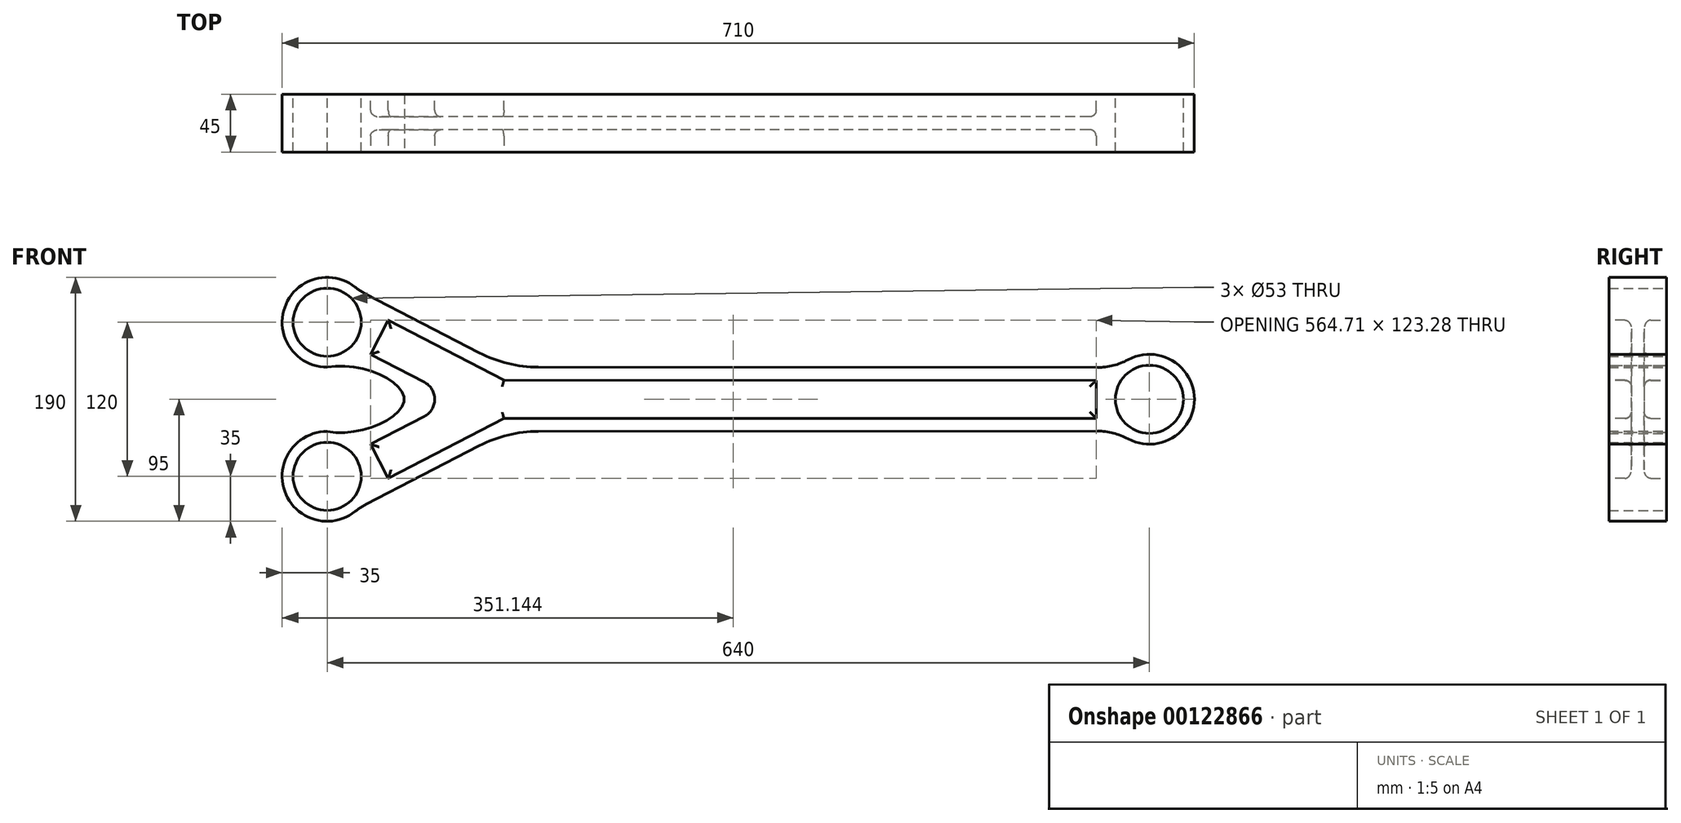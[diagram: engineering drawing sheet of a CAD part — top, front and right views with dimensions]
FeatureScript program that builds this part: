
annotation { "Feature Type Name" : "Feature", "Feature Type Description" : "" }
export const myFeature = defineFeature(function(context is Context, id is Id, definition is map)
    precondition{}
    {
        {
            var Q0;
            Q0=qCreatedBy(makeId("Front.planeOp"),FACE);
            var sketch = newSketch(context, id + "F0", { "sketchPlane" : qUnion([Q0])});
            skArc(sketch, "E0", {"start": v(-16.66, -30.78) * mm, "mid": v(35, 0) * mm, "end": v(-16.66, 30.78) * mm});
            skArc(sketch, "E1", {"start": v(-618.13, 87.33) * mm, "mid": v(-673.03, 71.59) * mm, "end": v(-640, 25) * mm});
            skCircle(sketch, "E2", {"center": v(-700, 0) * mm, "radius": 27.5 * mm, "construction": true});
            skCircle(sketch, "E3", {"center": v(-640, 60) * mm, "radius": 26.5 * mm});
            skCircle(sketch, "E4", {"center": v(-640, -60) * mm, "radius": 26.5 * mm});
            skCircle(sketch, "E5", {"center": v(0, 0) * mm, "radius": 26.5 * mm});
            skLineSegment(sketch, "E6", {"start": v(-40.48, 24.76) * mm, "end": v(-475.65, 24.99) * mm});
            skLineSegment(sketch, "E7", {"start": v(-40.48, -24.76) * mm, "end": v(-475.65, -24.99) * mm});
            skLineSegment(sketch, "E8", {"start": v(-521.62, -36.2) * mm, "end": v(-609.9, -81.98) * mm});
            skLineSegment(sketch, "E9", {"start": v(-521.62, 36.2) * mm, "end": v(-609.9, 81.98) * mm});
            skPoint(sketch, "E10.visualSharp", {"position": v(-500, 25) * mm});
            skArc(sketch, "E10.filletArc", {"start": v(-521.62, 36.2) * mm, "mid": v(-499.3, 27.84) * mm, "end": v(-475.65, 24.99) * mm});
            skPoint(sketch, "E11.visualSharp", {"position": v(-500, -25) * mm});
            skArc(sketch, "E11.filletArc", {"start": v(-475.65, -24.99) * mm, "mid": v(-499.3, -27.84) * mm, "end": v(-521.62, -36.2) * mm});
            skPoint(sketch, "E12.visualSharp", {"position": v(-615.25, 84.75) * mm});
            skArc(sketch, "E13", {"start": v(-640, -25) * mm, "mid": v(-673.03, -71.59) * mm, "end": v(-618.13, -87.33) * mm});
            skFitSpline(sketch, "E14", {"points": [v(-640, -25) * mm, v(-580, 0) * mm, v(-640, 25) * mm], "startDerivative": vector(150, -30) * mm, "endDerivative": vector(-150, -30) * mm});
            skPoint(sketch, "E15.visualSharp", {"position": v(-615.25, -84.75) * mm});
            skLineSegment(sketch, "E16", {"start": v(-24.75, 24.75) * mm, "end": v(0, 0) * mm, "construction": true});
            skLineSegment(sketch, "E17", {"start": v(-24.75, -24.75) * mm, "end": v(0, 0) * mm, "construction": true});
            skPoint(sketch, "E18.visualSharp", {"position": v(-24.75, 24.75) * mm});
            skArc(sketch, "E18.filletArc", {"start": v(-40.48, 24.76) * mm, "mid": v(-28.2, 26.28) * mm, "end": v(-16.66, 30.78) * mm});
            skPoint(sketch, "E19.visualSharp", {"position": v(-24.75, -24.75) * mm});
            skArc(sketch, "E19.filletArc", {"start": v(-16.66, -30.78) * mm, "mid": v(-28.2, -26.28) * mm, "end": v(-40.48, -24.76) * mm});
            skLineSegment(sketch, "E20", {"start": v(-615.25, 84.75) * mm, "end": v(-640, 60) * mm, "construction": true});
            skLineSegment(sketch, "E21", {"start": v(-640, -60) * mm, "end": v(-640, 177.49) * mm, "construction": true});
            skArc(sketch, "E22.filletArc", {"start": v(-618.13, 87.33) * mm, "mid": v(-614.15, 84.45) * mm, "end": v(-609.9, 81.98) * mm});
            skLineSegment(sketch, "E23", {"start": v(-615.25, -84.75) * mm, "end": v(-640, -60) * mm, "construction": true});
            skArc(sketch, "E24.filletArc", {"start": v(-609.9, -81.98) * mm, "mid": v(-614.15, -84.45) * mm, "end": v(-618.13, -87.33) * mm});
            skSolve(sketch);
        }
        {
            var Q0;
            Q0=qSketchRegion(id+"F0",true);
            extrude(context, id + "F1", {"entities" : qUnion([Q0]), "depth" : 45 * mm});
        }
        {
            var Q0;
            Q0=makeQuery(id+"F1.opExtrude","SWEPT_BODY",BODY,{"disambiguationData":[OSD([sQuery(id+"F0.wireOp",EDGE,"E0"),sQuery(id+"F0.wireOp",EDGE,"E1"),sQuery(id+"F0.wireOp",EDGE,"hKVllitM-rUlu-PjKN-B9u5-COeOs3Kio4uB"),sQuery(id+"F0.wireOp",EDGE,"bIEpRebq-8nbQ-7rQF-Jdrm-i3E8cfRsBNN9"),sQuery(id+"F0.wireOp",EDGE,"ymSRshFr-buK2-GFJu-27zL-H9ECYoIg19t0"),sQuery(id+"F0.wireOp",EDGE,"e6450e41-44a2-4cb5-af14-4686bec827bc"),sQuery(id+"F0.wireOp",EDGE,"ipdW7DlG-pZfv-p4Vr-qYAQ-uRQYnpMPVyQN"),sQuery(id+"F0.wireOp",EDGE,"9qNpO7d9-6r7V-397W-DIXA-CVevZtzhY8f4"),sQuery(id+"F0.wireOp",EDGE,"E3"),sQuery(id+"F0.wireOp",EDGE,"E4"),sQuery(id+"F0.wireOp",EDGE,"E5")])]});
            var Q1;
            Q1=makeQuery(id+"F1.opExtrude","CAP_EDGE",EDGE,{"disambiguationData":[OSD([sQuery(id+"F0.wireOp",EDGE,"E5")])],"isStart":false});
            transform(context, id + "F2", {"entities" : qUnion([Q0]), "transformType" : TransformType.ROTATION, "transformAxis" : qUnion([Q1]), "angle" : 12.5 * degree, "makeCopy" : true});
        }
        {
            var Q0;
            Q0=makeQuery(id+"F1.opExtrude","CAP_FACE",FACE,{"disambiguationData":[OSD([sQuery(id+"F0.wireOp",EDGE,"E0"),sQuery(id+"F0.wireOp",EDGE,"E1"),sQuery(id+"F0.wireOp",EDGE,"E3"),sQuery(id+"F0.wireOp",EDGE,"E4"),sQuery(id+"F0.wireOp",EDGE,"E5"),sQuery(id+"F0.wireOp",EDGE,"E6"),sQuery(id+"F0.wireOp",EDGE,"E7"),sQuery(id+"F0.wireOp",EDGE,"E8"),sQuery(id+"F0.wireOp",EDGE,"E9"),sQuery(id+"F0.wireOp",EDGE,"E10.filletArc"),sQuery(id+"F0.wireOp",EDGE,"E11.filletArc"),sQuery(id+"F0.wireOp",EDGE,"E13"),sQuery(id+"F0.wireOp",EDGE,"E14"),sQuery(id+"F0.wireOp",EDGE,"E18.filletArc"),sQuery(id+"F0.wireOp",EDGE,"E19.filletArc"),sQuery(id+"F0.wireOp",EDGE,"E22.filletArc"),sQuery(id+"F0.wireOp",EDGE,"E24.filletArc")])],"isStart":false});
            var sketch = newSketch(context, id + "F3", { "sketchPlane" : qUnion([Q0])});
            skLineSegment(sketch, "E25", {"start": v(-41.5, 14.76) * mm, "end": v(-502.44, 15) * mm});
            skLineSegment(sketch, "E26", {"start": v(-41.5, -14.76) * mm, "end": v(-502.44, -15) * mm});
            skLineSegment(sketch, "E27", {"start": v(-502.44, -15) * mm, "end": v(-592.4, -61.64) * mm});
            skLineSegment(sketch, "E28", {"start": v(-592.4, -61.64) * mm, "end": v(-606.21, -35) * mm});
            skLineSegment(sketch, "E29", {"start": v(-606.21, -35) * mm, "end": v(-564.37, -13.32) * mm});
            skLineSegment(sketch, "E30", {"start": v(-502.44, 15) * mm, "end": v(-592.4, 61.64) * mm});
            skLineSegment(sketch, "E31", {"start": v(-592.4, 61.64) * mm, "end": v(-606.21, 35) * mm});
            skLineSegment(sketch, "E32", {"start": v(-606.21, 35) * mm, "end": v(-564.37, 13.32) * mm});
            skPoint(sketch, "E33.visualSharp", {"position": v(-538.69, 0) * mm});
            skArc(sketch, "E33.filletArc", {"start": v(-564.37, -13.32) * mm, "mid": v(-556.28, 0) * mm, "end": v(-564.37, 13.32) * mm});
            skLineSegment(sketch, "E34", {"start": v(-41.5, 14.76) * mm, "end": v(-41.5, -14.76) * mm});
            skSolve(sketch);
        }
        {
            var Q0;
            Q0=qSketchRegion(id+"F3",true);
            extrude(context, id + "F4", {"entities" : qUnion([Q0]), "operationType" : NewBodyOperationType.REMOVE, "oppositeDirection" : true, "depth" : 17.5 * mm});
        }
        {
            var Q0;
            Q0=makeQuery(id+"F1.opExtrude","CAP_FACE",FACE,{"disambiguationData":[OSD([sQuery(id+"F0.wireOp",EDGE,"E0"),sQuery(id+"F0.wireOp",EDGE,"E1"),sQuery(id+"F0.wireOp",EDGE,"E3"),sQuery(id+"F0.wireOp",EDGE,"E4"),sQuery(id+"F0.wireOp",EDGE,"E5"),sQuery(id+"F0.wireOp",EDGE,"E6"),sQuery(id+"F0.wireOp",EDGE,"E7"),sQuery(id+"F0.wireOp",EDGE,"E8"),sQuery(id+"F0.wireOp",EDGE,"E9"),sQuery(id+"F0.wireOp",EDGE,"E10.filletArc"),sQuery(id+"F0.wireOp",EDGE,"E11.filletArc"),sQuery(id+"F0.wireOp",EDGE,"E13"),sQuery(id+"F0.wireOp",EDGE,"E14"),sQuery(id+"F0.wireOp",EDGE,"E18.filletArc"),sQuery(id+"F0.wireOp",EDGE,"E19.filletArc"),sQuery(id+"F0.wireOp",EDGE,"E22.filletArc"),sQuery(id+"F0.wireOp",EDGE,"E24.filletArc")])],"isStart":true});
            var sketch = newSketch(context, id + "F5", { "sketchPlane" : qUnion([Q0])});
            skLineSegment(sketch, "E35", {"start": v(41.5, 14.76) * mm, "end": v(502.44, 15) * mm});
            skLineSegment(sketch, "E36", {"start": v(502.44, 15) * mm, "end": v(592.4, 61.64) * mm});
            skLineSegment(sketch, "E37", {"start": v(592.4, 61.64) * mm, "end": v(606.21, 35) * mm});
            skLineSegment(sketch, "E38", {"start": v(606.21, -35) * mm, "end": v(592.4, -61.64) * mm});
            skLineSegment(sketch, "E39", {"start": v(592.4, -61.64) * mm, "end": v(502.44, -15) * mm});
            skLineSegment(sketch, "E40", {"start": v(502.44, -15) * mm, "end": v(41.5, -14.76) * mm});
            skLineSegment(sketch, "E41", {"start": v(41.5, 14.76) * mm, "end": v(41.5, -14.76) * mm});
            skLineSegment(sketch, "E42", {"start": v(606.21, 35) * mm, "end": v(564.37, 13.32) * mm});
            skLineSegment(sketch, "E43", {"start": v(564.37, -13.32) * mm, "end": v(606.21, -35) * mm});
            skPoint(sketch, "E44.visualSharp", {"position": v(538.69, 0) * mm});
            skArc(sketch, "E44.filletArc", {"start": v(564.37, 13.32) * mm, "mid": v(556.28, 0) * mm, "end": v(564.37, -13.32) * mm});
            skSolve(sketch);
        }
        {
            var Q0;
            Q0=qSketchRegion(id+"F5",true);
            extrude(context, id + "F6", {"entities" : qUnion([Q0]), "operationType" : NewBodyOperationType.REMOVE, "oppositeDirection" : true, "depth" : 17.5 * mm});
        }
        {
            var Q0;
            Q0=makeQuery(id+"F6.boolean.opBoolean","COPY",EDGE,{"derivedFrom":makeQuery(id+"F6.opExtrude","CAP_EDGE",EDGE,{"disambiguationData":[OSD([sQuery(id+"F5.wireOp",EDGE,"E35")])],"isStart":false})});
            var Q1;
            Q1=makeQuery(id+"F6.boolean.opBoolean","COPY",EDGE,{"derivedFrom":makeQuery(id+"F6.opExtrude","CAP_EDGE",EDGE,{"disambiguationData":[OSD([sQuery(id+"F5.wireOp",EDGE,"E41")])],"isStart":false})});
            var Q2;
            Q2=makeQuery(id+"F6.boolean.opBoolean","COPY",EDGE,{"derivedFrom":makeQuery(id+"F6.opExtrude","CAP_EDGE",EDGE,{"disambiguationData":[OSD([sQuery(id+"F5.wireOp",EDGE,"E40")])],"isStart":false})});
            var Q3;
            Q3=makeQuery(id+"F6.boolean.opBoolean","COPY",EDGE,{"derivedFrom":makeQuery(id+"F6.opExtrude","CAP_EDGE",EDGE,{"disambiguationData":[OSD([sQuery(id+"F5.wireOp",EDGE,"E36")])],"isStart":false})});
            var Q4;
            Q4=makeQuery(id+"F6.boolean.opBoolean","COPY",EDGE,{"derivedFrom":makeQuery(id+"F6.opExtrude","CAP_EDGE",EDGE,{"disambiguationData":[OSD([sQuery(id+"F5.wireOp",EDGE,"E39")])],"isStart":false})});
            var Q5;
            Q5=makeQuery(id+"F6.boolean.opBoolean","COPY",EDGE,{"derivedFrom":makeQuery(id+"F6.opExtrude","CAP_EDGE",EDGE,{"disambiguationData":[OSD([sQuery(id+"F5.wireOp",EDGE,"E38")])],"isStart":false})});
            var Q6;
            Q6=makeQuery(id+"F6.boolean.opBoolean","COPY",EDGE,{"derivedFrom":makeQuery(id+"F6.opExtrude","CAP_EDGE",EDGE,{"disambiguationData":[OSD([sQuery(id+"F5.wireOp",EDGE,"E43")])],"isStart":false})});
            var Q7;
            Q7=makeQuery(id+"F6.boolean.opBoolean","COPY",EDGE,{"derivedFrom":makeQuery(id+"F6.opExtrude","CAP_EDGE",EDGE,{"disambiguationData":[OSD([sQuery(id+"F5.wireOp",EDGE,"E37")])],"isStart":false})});
            fillet(context, id + "F7", {"entities" : qUnion([Q0, Q1, Q2, Q3, Q4, Q5, Q6, Q7]), "radius" : 5 * mm, "tangentPropagation" : true, "allowEdgeOverflow" : false});
        }
        {
            var Q0;
            Q0=makeQuery(id+"F4.boolean.opBoolean","COPY",EDGE,{"derivedFrom":makeQuery(id+"F4.opExtrude","CAP_EDGE",EDGE,{"disambiguationData":[OSD([sQuery(id+"F3.wireOp",EDGE,"E28")])],"isStart":false})});
            var Q1;
            Q1=makeQuery(id+"F4.boolean.opBoolean","COPY",EDGE,{"derivedFrom":makeQuery(id+"F4.opExtrude","CAP_EDGE",EDGE,{"disambiguationData":[OSD([sQuery(id+"F3.wireOp",EDGE,"E27")])],"isStart":false})});
            var Q2;
            Q2=makeQuery(id+"F4.boolean.opBoolean","COPY",EDGE,{"derivedFrom":makeQuery(id+"F4.opExtrude","CAP_EDGE",EDGE,{"disambiguationData":[OSD([sQuery(id+"F3.wireOp",EDGE,"E26")])],"isStart":false})});
            var Q3;
            Q3=makeQuery(id+"F4.boolean.opBoolean","COPY",EDGE,{"derivedFrom":makeQuery(id+"F4.opExtrude","CAP_EDGE",EDGE,{"disambiguationData":[OSD([sQuery(id+"F3.wireOp",EDGE,"E32")])],"isStart":false})});
            var Q4;
            Q4=makeQuery(id+"F4.boolean.opBoolean","COPY",EDGE,{"derivedFrom":makeQuery(id+"F4.opExtrude","CAP_EDGE",EDGE,{"disambiguationData":[OSD([sQuery(id+"F3.wireOp",EDGE,"E31")])],"isStart":false})});
            var Q5;
            Q5=makeQuery(id+"F4.boolean.opBoolean","COPY",EDGE,{"derivedFrom":makeQuery(id+"F4.opExtrude","CAP_EDGE",EDGE,{"disambiguationData":[OSD([sQuery(id+"F3.wireOp",EDGE,"E30")])],"isStart":false})});
            var Q6;
            Q6=makeQuery(id+"F4.boolean.opBoolean","COPY",EDGE,{"derivedFrom":makeQuery(id+"F4.opExtrude","CAP_EDGE",EDGE,{"disambiguationData":[OSD([sQuery(id+"F3.wireOp",EDGE,"E25")])],"isStart":false})});
            var Q7;
            Q7=makeQuery(id+"F4.boolean.opBoolean","COPY",EDGE,{"derivedFrom":makeQuery(id+"F4.opExtrude","CAP_EDGE",EDGE,{"disambiguationData":[OSD([sQuery(id+"F3.wireOp",EDGE,"E34")])],"isStart":false})});
            fillet(context, id + "F8", {"entities" : qUnion([Q0, Q1, Q2, Q3, Q4, Q5, Q6, Q7]), "radius" : 5 * mm, "tangentPropagation" : true, "allowEdgeOverflow" : false});
        }
        {
            var Q0;
            Q0=makeQuery(id+"F2.opPattern","COPY",BODY,{"derivedFrom":makeQuery(id+"F1.opExtrude","SWEPT_BODY",BODY,{"disambiguationData":[OSD([sQuery(id+"F0.wireOp",EDGE,"E0"),sQuery(id+"F0.wireOp",EDGE,"E1"),sQuery(id+"F0.wireOp",EDGE,"E3"),sQuery(id+"F0.wireOp",EDGE,"E4"),sQuery(id+"F0.wireOp",EDGE,"E5"),sQuery(id+"F0.wireOp",EDGE,"E6"),sQuery(id+"F0.wireOp",EDGE,"E7"),sQuery(id+"F0.wireOp",EDGE,"E8"),sQuery(id+"F0.wireOp",EDGE,"E9"),sQuery(id+"F0.wireOp",EDGE,"E10.filletArc"),sQuery(id+"F0.wireOp",EDGE,"E11.filletArc"),sQuery(id+"F0.wireOp",EDGE,"E13"),sQuery(id+"F0.wireOp",EDGE,"E14"),sQuery(id+"F0.wireOp",EDGE,"E18.filletArc"),sQuery(id+"F0.wireOp",EDGE,"E19.filletArc"),sQuery(id+"F0.wireOp",EDGE,"E22.filletArc"),sQuery(id+"F0.wireOp",EDGE,"E24.filletArc")])]}),"instanceName":"1"});
            deleteBodies(context, id + "F9", {"entities" : qUnion([Q0])});
        }
    });
